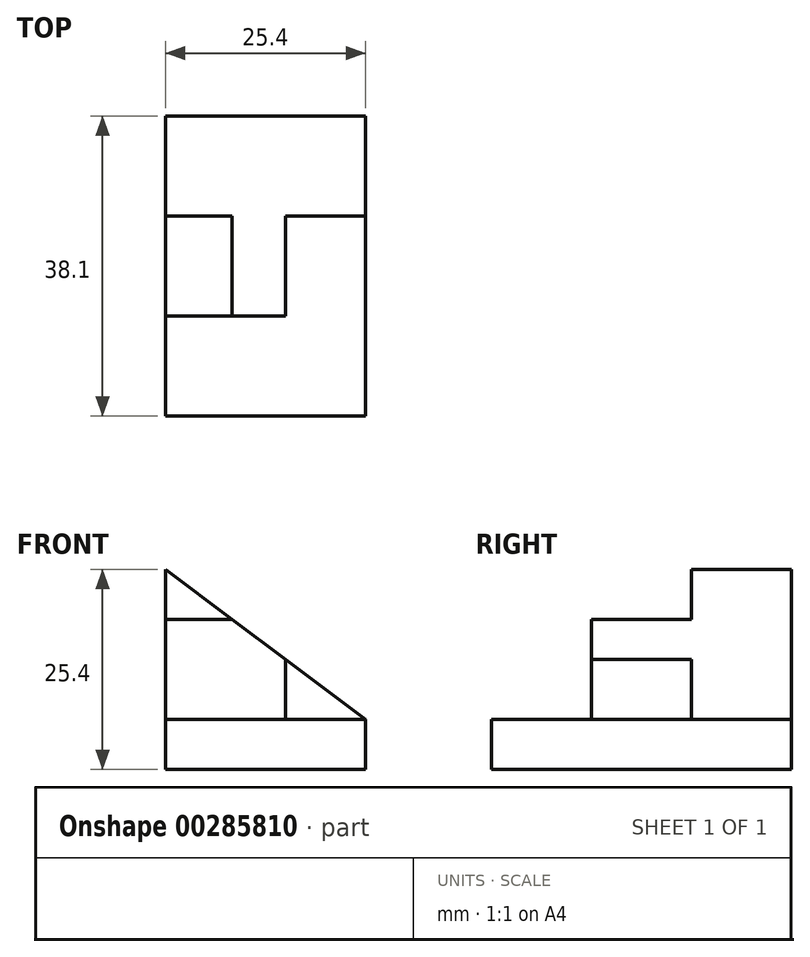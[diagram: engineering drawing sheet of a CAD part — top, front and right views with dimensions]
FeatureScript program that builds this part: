
annotation { "Feature Type Name" : "Feature", "Feature Type Description" : "" }
export const myFeature = defineFeature(function(context is Context, id is Id, definition is map)
    precondition{}
    {
        {
            var Q0;
            Q0=qCreatedBy(makeId("Front.planeOp"),FACE);
            var sketch = newSketch(context, id + "F0", { "sketchPlane" : qUnion([Q0])});
            skLineSegment(sketch, "E0.bottom", {"start": v(0, 0) * mm, "end": v(25.4, 0) * mm});
            skLineSegment(sketch, "E0.top", {"start": v(0, 6.35) * mm, "end": v(25.4, 6.35) * mm});
            skLineSegment(sketch, "E0.left", {"start": v(0, 0) * mm, "end": v(0, 6.35) * mm});
            skLineSegment(sketch, "E0.right", {"start": v(25.4, 0) * mm, "end": v(25.4, 6.35) * mm});
            skSolve(sketch);
        }
        {
            var Q0;
            Q0=makeQuery(id+"F0.imprint","IMPRINT",FACE,{"disambiguationData":[TD([[makeQuery(id+"F0.imprint","IMPRINT",EDGE,{"derivedFrom":sQuery(id+"F0.wireOp",EDGE,"E0.bottom")}),1.0]])]});
            extrude(context, id + "F1", {"entities" : qUnion([Q0]), "depth" : 38.1 * mm, "symmetric" : true});
        }
        {
            var Q0;
            Q0=makeQuery(id+"F1.opExtrude","CAP_FACE",FACE,{"disambiguationData":[OSD([sQuery(id+"F0.wireOp",EDGE,"E0.bottom"),sQuery(id+"F0.wireOp",EDGE,"E0.top"),sQuery(id+"F0.wireOp",EDGE,"E0.left"),sQuery(id+"F0.wireOp",EDGE,"E0.right")])],"isStart":true});
            var sketch = newSketch(context, id + "F2", { "sketchPlane" : qUnion([Q0])});
            skLineSegment(sketch, "E1", {"start": v(0, 6.35) * mm, "end": v(0, 25.4) * mm});
            skLineSegment(sketch, "E2", {"start": v(0, 25.4) * mm, "end": v(-25.4, 6.35) * mm});
            skSolve(sketch);
        }
        {
            var Q0;
            Q0=makeQuery(id+"F2.imprint","IMPRINT",FACE,{"disambiguationData":[TD([[makeQuery(id+"F2.imprint","IMPRINT",EDGE,{"derivedFrom":sQuery(id+"F2.wireOp",EDGE,"E1")}),1.0]])]});
            extrude(context, id + "F3", {"entities" : qUnion([Q0]), "operationType" : NewBodyOperationType.ADD, "oppositeDirection" : true, "depth" : 12.7 * mm});
        }
        {
            var Q0;
            Q0=makeQuery(id+"F3.boolean.opBoolean","MERGE",FACE,{"derivedFrom":[makeQuery(id+"F1.opExtrude","SWEPT_FACE",FACE,{"disambiguationData":[OSD([sQuery(id+"F0.wireOp",EDGE,"E0.left")])]}),makeQuery(id+"F3.opExtrude","SWEPT_FACE",FACE,{"disambiguationData":[OSD([sQuery(id+"F2.wireOp",EDGE,"E1")])]})]});
            var sketch = newSketch(context, id + "F4", { "sketchPlane" : qUnion([Q0])});
            skLineSegment(sketch, "E3", {"start": v(-6.35, 6.35) * mm, "end": v(6.35, 6.35) * mm});
            skLineSegment(sketch, "E4", {"start": v(6.35, 6.35) * mm, "end": v(6.35, 19.05) * mm});
            skLineSegment(sketch, "E5", {"start": v(6.35, 19.05) * mm, "end": v(-6.35, 19.05) * mm});
            skLineSegment(sketch, "E6", {"start": v(-6.35, 19.05) * mm, "end": v(-6.35, 6.35) * mm});
            skSolve(sketch);
        }
        {
            var Q0;
            Q0=makeQuery(id+"F4.imprint","IMPRINT",FACE,{"disambiguationData":[TD([[makeQuery(id+"F4.imprint","IMPRINT",EDGE,{"derivedFrom":sQuery(id+"F4.wireOp",EDGE,"E3")}),-1.0]])]});
            extrude(context, id + "F5", {"entities" : qUnion([Q0]), "operationType" : NewBodyOperationType.ADD, "oppositeDirection" : true, "depth" : 15.24 * mm});
        }
        {
            var Q0;
            Q0=makeQuery(id+"F5.opExtrude","SWEPT_FACE",FACE,{"disambiguationData":[OSD([sQuery(id+"F4.wireOp",EDGE,"E6")])]});
            extrude(context, id + "F6", {"entities" : qUnion([Q0]), "operationType" : NewBodyOperationType.REMOVE, "oppositeDirection" : true, "depth" : 25.4 * mm});
        }
    });
